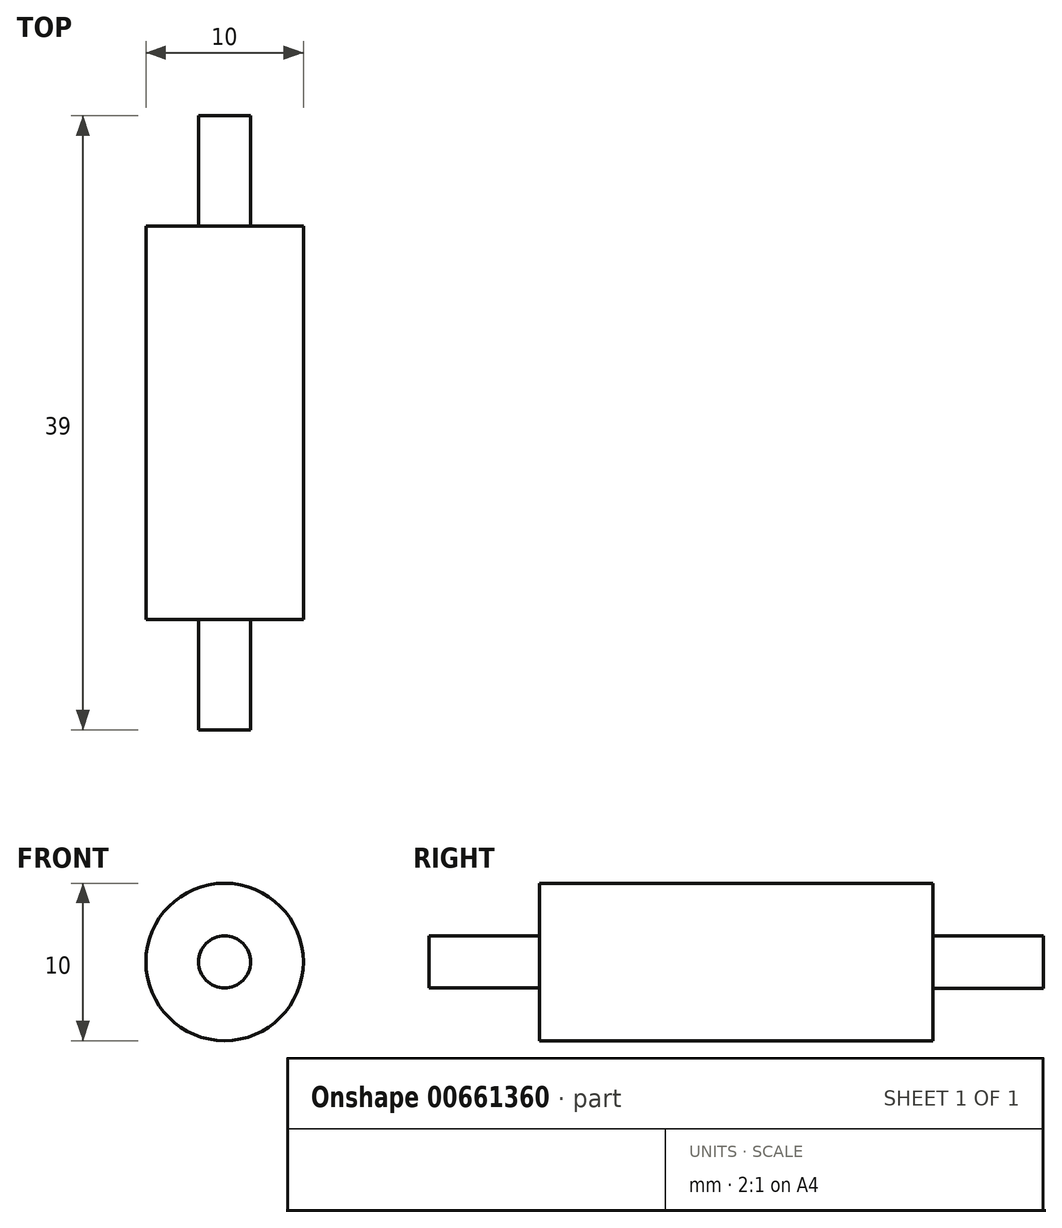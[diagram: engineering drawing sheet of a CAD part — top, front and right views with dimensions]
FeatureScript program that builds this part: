
annotation { "Feature Type Name" : "Feature", "Feature Type Description" : "" }
export const myFeature = defineFeature(function(context is Context, id is Id, definition is map)
    precondition{}
    {
        {
            var Q0;
            Q0=qCreatedBy(makeId("Front.planeOp"),FACE);
            var sketch = newSketch(context, id + "F0", { "sketchPlane" : qUnion([Q0])});
            skCircle(sketch, "E0", {"center": v(-47.55, 33.9) * mm, "radius": 5 * mm});
            skSolve(sketch);
        }
        {
            var Q0;
            Q0 = qSketchRegion(id + "F0", true);
            extrude(context, id + "F1", {"entities" : qUnion([Q0]), "depth" : 25 * mm, "offsetDistance" : 25 * mm});
        }
        {
            var Q0;
            Q0=makeQuery(id+"F1.opExtrude","CAP_FACE",FACE,{"disambiguationData":[OSD([sQuery(id+"F0.wireOp",EDGE,"E0")])],"isStart":false});
            var sketch = newSketch(context, id + "F2", { "sketchPlane" : qUnion([Q0])});
            skCircle(sketch, "E1", {"center": v(-47.55, 33.9) * mm, "radius": 1.65 * mm});
            skSolve(sketch);
        }
        {
            var Q0;
            Q0 = qSketchRegion(id + "F2", true);
            var Q1;
            Q1=sQuery(id+"F2.wireOp",EDGE,"E1");
            extrude(context, id + "F3", {"entities" : qUnion([Q0]), "operationType" : NewBodyOperationType.ADD, "surfaceEntities" : qUnion([Q1]), "depth" : 7 * mm, "offsetDistance" : 25 * mm});
        }
        {
            var Q0;
            Q0=makeQuery(id+"F1.opExtrude","CAP_FACE",FACE,{"disambiguationData":[OSD([sQuery(id+"F0.wireOp",EDGE,"E0")])],"isStart":true});
            var sketch = newSketch(context, id + "F4", { "sketchPlane" : qUnion([Q0])});
            skCircle(sketch, "E2", {"center": v(47.55, 33.9) * mm, "radius": 1.67 * mm});
            skSolve(sketch);
        }
        {
            var Q0;
            Q0 = qSketchRegion(id + "F4", true);
            extrude(context, id + "F5", {"entities" : qUnion([Q0]), "operationType" : NewBodyOperationType.ADD, "depth" : 7 * mm, "offsetDistance" : 25 * mm});
        }
    });
